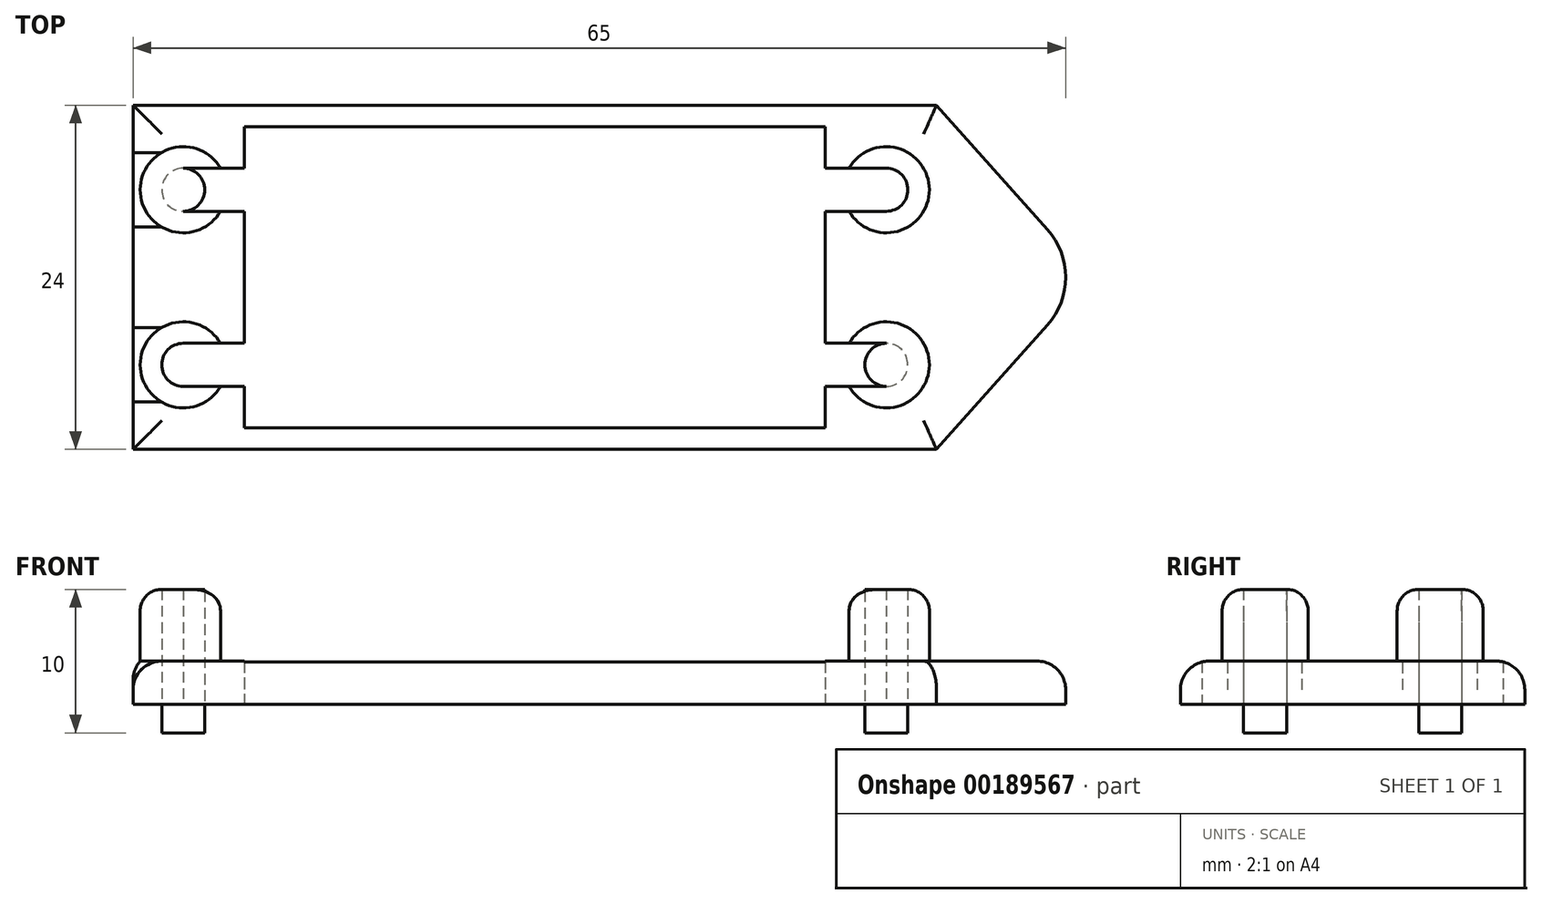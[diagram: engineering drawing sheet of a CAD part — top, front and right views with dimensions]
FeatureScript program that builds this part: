
annotation { "Feature Type Name" : "Feature", "Feature Type Description" : "" }
export const myFeature = defineFeature(function(context is Context, id is Id, definition is map)
    precondition{}
    {
        {
            var Q0;
            Q0=qCreatedBy(makeId("Top.planeOp"),FACE);
            var sketch = newSketch(context, id + "F0", { "sketchPlane" : qUnion([Q0])});
            skLineSegment(sketch, "E0.bottom", {"start": v(20.25, -10.5) * mm, "end": v(-20.25, -10.5) * mm});
            skLineSegment(sketch, "E0.top", {"start": v(20.25, 10.5) * mm, "end": v(-20.25, 10.5) * mm});
            skLineSegment(sketch, "E0.left", {"start": v(20.25, -10.5) * mm, "end": v(20.25, -7.6) * mm});
            skLineSegment(sketch, "E0.right", {"start": v(-20.25, -10.5) * mm, "end": v(-20.25, -7.6) * mm});
            skPoint(sketch, "E0.middle", {"position": v(0, 0) * mm});
            skArc(sketch, "E1", {"start": v(-24.5, 7.6) * mm, "mid": v(-26, 6.1) * mm, "end": v(-24.5, 4.6) * mm});
            skLineSegment(sketch, "E2", {"start": v(-24.5, 4.6) * mm, "end": v(-20.25, 4.6) * mm});
            skLineSegment(sketch, "E3", {"start": v(-20.25, 7.6) * mm, "end": v(-24.5, 7.6) * mm});
            skLineSegment(sketch, "E4.trimOffspring", {"start": v(-20.25, 7.6) * mm, "end": v(-20.25, 10.5) * mm});
            skLineSegment(sketch, "E5.MirrorCS", {"start": v(20.25, 7.6) * mm, "end": v(24.5, 7.6) * mm});
            skLineSegment(sketch, "E6.MirrorCS", {"start": v(20.25, 7.6) * mm, "end": v(20.25, 10.5) * mm});
            skLineSegment(sketch, "E7.MirrorCS", {"start": v(24.5, 4.6) * mm, "end": v(20.25, 4.6) * mm});
            skArc(sketch, "E8.MirrorCS", {"start": v(24.5, 7.6) * mm, "mid": v(26, 6.1) * mm, "end": v(24.5, 4.6) * mm});
            skLineSegment(sketch, "E9.MirrorCS", {"start": v(24.5, -4.6) * mm, "end": v(20.25, -4.6) * mm});
            skArc(sketch, "E10.MirrorCS", {"start": v(24.5, -7.6) * mm, "mid": v(26, -6.1) * mm, "end": v(24.5, -4.6) * mm});
            skLineSegment(sketch, "E11.MirrorCS", {"start": v(20.25, -7.6) * mm, "end": v(24.5, -7.6) * mm});
            skLineSegment(sketch, "E12.MirrorCS", {"start": v(-20.25, 10.5) * mm, "end": v(-20.25, 7.6) * mm});
            skLineSegment(sketch, "E13.MirrorCS", {"start": v(-20.25, -7.6) * mm, "end": v(-24.5, -7.6) * mm});
            skLineSegment(sketch, "E14.MirrorCS", {"start": v(-24.5, -4.6) * mm, "end": v(-20.25, -4.6) * mm});
            skArc(sketch, "E15.MirrorCS", {"start": v(-24.5, -7.6) * mm, "mid": v(-26, -6.1) * mm, "end": v(-24.5, -4.6) * mm});
            skLineSegment(sketch, "E16.MirrorCS", {"start": v(-20.25, -7.6) * mm, "end": v(-20.25, -10.5) * mm});
            skLineSegment(sketch, "E17.trimOffspring", {"start": v(20.25, -4.6) * mm, "end": v(20.25, 4.6) * mm});
            skLineSegment(sketch, "E18.trimOffspring", {"start": v(-20.25, -4.6) * mm, "end": v(-20.25, 4.6) * mm});
            skLineSegment(sketch, "E19.trimOffspring", {"start": v(-20.25, 4.6) * mm, "end": v(-20.25, -4.6) * mm});
            skSolve(sketch);
        }
        {
            var Q0;
            Q0=makeQuery(id+"F0.imprint","IMPRINT",FACE,{"disambiguationData":[TD([[makeQuery(id+"F0.imprint","IMPRINT",EDGE,{"derivedFrom":sQuery(id+"F0.wireOp",EDGE,"E0.bottom")}),-1.0]])]});
            extrude(context, id + "F1", {"entities" : qUnion([Q0]), "depth" : 2 * mm});
        }
        {
            var Q0;
            Q0=makeQuery(id+"F1.opExtrude","CAP_FACE",FACE,{"disambiguationData":[OSD([sQuery(id+"F0.wireOp",EDGE,"E0.bottom"),sQuery(id+"F0.wireOp",EDGE,"E0.top"),sQuery(id+"F0.wireOp",EDGE,"E0.left"),sQuery(id+"F0.wireOp",EDGE,"E0.right")])],"isStart":false});
            var sketch = newSketch(context, id + "F2", { "sketchPlane" : qUnion([Q0])});
            skLineSegment(sketch, "E20.bottom", {"start": v(28, -12) * mm, "end": v(-28, -12) * mm});
            skLineSegment(sketch, "E20.top", {"start": v(28, 12) * mm, "end": v(-28, 12) * mm});
            skLineSegment(sketch, "E20.right", {"start": v(-28, -12) * mm, "end": v(-28, 12) * mm});
            skPoint(sketch, "E20.middle", {"position": v(0, 0) * mm});
            skCircle(sketch, "E21", {"center": v(32, 0) * mm, "radius": 1 * mm, "construction": true});
            skArc(sketch, "E22", {"start": v(35.73, -3.33) * mm, "mid": v(37, 0) * mm, "end": v(35.73, 3.33) * mm});
            skLineSegment(sketch, "E23", {"start": v(28, -12) * mm, "end": v(35.73, -3.33) * mm});
            skLineSegment(sketch, "E24", {"start": v(28, 12) * mm, "end": v(35.73, 3.33) * mm});
            skSolve(sketch);
        }
        {
            var Q0;
            Q0=makeQuery(id+"F2.imprint","IMPRINT",FACE,{"disambiguationData":[TD([[makeQuery(id+"F2.imprint","IMPRINT",EDGE,{"derivedFrom":sQuery(id+"F2.wireOp",EDGE,"E20.bottom")}),-1.0]])]});
            var Q1;
            Q1=makeQuery(id+"F2.imprint","IMPRINT",FACE,{"disambiguationData":[TD([[makeQuery(id+"F2.imprint","IMPRINT",EDGE,{"derivedFrom":makeQuery(id+"F1.opExtrude","CAP_EDGE",EDGE,{"disambiguationData":[OSD([sQuery(id+"F0.wireOp",EDGE,"E0.bottom")])],"isStart":false})}),-1.0]])]});
            extrude(context, id + "F3", {"entities" : qUnion([Q0, Q1]), "operationType" : NewBodyOperationType.ADD, "depth" : 3 * mm});
        }
        {
            var Q0;
            Q0=makeQuery(id+"F1.opExtrude","CAP_FACE",FACE,{"disambiguationData":[OSD([sQuery(id+"F0.wireOp",EDGE,"E0.bottom"),sQuery(id+"F0.wireOp",EDGE,"E0.top"),sQuery(id+"F0.wireOp",EDGE,"E1"),sQuery(id+"F0.wireOp",EDGE,"E2"),sQuery(id+"F0.wireOp",EDGE,"E3"),sQuery(id+"F0.wireOp",EDGE,"E5.MirrorCS"),sQuery(id+"F0.wireOp",EDGE,"E7.MirrorCS"),sQuery(id+"F0.wireOp",EDGE,"E0.left"),sQuery(id+"F0.wireOp",EDGE,"E8.MirrorCS"),sQuery(id+"F0.wireOp",EDGE,"E9.MirrorCS"),sQuery(id+"F0.wireOp",EDGE,"E10.MirrorCS"),sQuery(id+"F0.wireOp",EDGE,"E11.MirrorCS"),sQuery(id+"F0.wireOp",EDGE,"E12.MirrorCS"),sQuery(id+"F0.wireOp",EDGE,"E13.MirrorCS"),sQuery(id+"F0.wireOp",EDGE,"E14.MirrorCS"),sQuery(id+"F0.wireOp",EDGE,"E15.MirrorCS"),sQuery(id+"F0.wireOp",EDGE,"E16.MirrorCS"),sQuery(id+"F0.wireOp",EDGE,"E6.MirrorCS"),sQuery(id+"F0.wireOp",EDGE,"E17.trimOffspring"),sQuery(id+"F0.wireOp",EDGE,"E19.trimOffspring")])],"isStart":true});
            var sketch = newSketch(context, id + "F4", { "sketchPlane" : qUnion([Q0])});
            skCircle(sketch, "E25", {"center": v(24.5, -6.1) * mm, "radius": 1.5 * mm});
            skCircle(sketch, "E26", {"center": v(24.5, 6.1) * mm, "radius": 1.5 * mm});
            skCircle(sketch, "E27", {"center": v(-24.5, -6.1) * mm, "radius": 1.5 * mm});
            skCircle(sketch, "E28", {"center": v(-24.5, 6.1) * mm, "radius": 1.5 * mm});
            skSolve(sketch);
        }
        {
            var Q0;
            Q0=makeQuery(id+"F3.opExtrude","CAP_FACE",FACE,{"disambiguationData":[OSD([sQuery(id+"F2.wireOp",EDGE,"E20.bottom"),sQuery(id+"F2.wireOp",EDGE,"E20.top"),sQuery(id+"F2.wireOp",EDGE,"E20.right"),sQuery(id+"F2.wireOp",EDGE,"E22"),sQuery(id+"F2.wireOp",EDGE,"E23"),sQuery(id+"F2.wireOp",EDGE,"E24")])],"isStart":false});
            var sketch = newSketch(context, id + "F5", { "sketchPlane" : qUnion([Q0])});
            skCircle(sketch, "E29", {"center": v(-24.5, 6.1) * mm, "radius": 3 * mm});
            skCircle(sketch, "E30", {"center": v(-24.5, -6.1) * mm, "radius": 3 * mm});
            skCircle(sketch, "E31", {"center": v(24.5, 6.1) * mm, "radius": 3 * mm});
            skCircle(sketch, "E32", {"center": v(24.5, -6.1) * mm, "radius": 3 * mm});
            skSolve(sketch);
        }
        {
            var Q0;
            Q0=makeQuery(id+"F5.imprint","IMPRINT",FACE,{"disambiguationData":[TD([[makeQuery(id+"F5.imprint","IMPRINT",EDGE,{"derivedFrom":sQuery(id+"F5.wireOp",EDGE,"E29")}),1.0]])]});
            var Q1;
            Q1=makeQuery(id+"F5.imprint","IMPRINT",FACE,{"disambiguationData":[TD([[makeQuery(id+"F5.imprint","IMPRINT",EDGE,{"derivedFrom":sQuery(id+"F5.wireOp",EDGE,"E30")}),1.0]])]});
            var Q2;
            Q2=makeQuery(id+"F5.imprint","IMPRINT",FACE,{"disambiguationData":[TD([[makeQuery(id+"F5.imprint","IMPRINT",EDGE,{"derivedFrom":sQuery(id+"F5.wireOp",EDGE,"E32")}),1.0]])]});
            var Q3;
            Q3=makeQuery(id+"F5.imprint","IMPRINT",FACE,{"disambiguationData":[TD([[makeQuery(id+"F5.imprint","IMPRINT",EDGE,{"derivedFrom":sQuery(id+"F5.wireOp",EDGE,"E31")}),1.0]])]});
            extrude(context, id + "F6", {"entities" : qUnion([Q0, Q1, Q2, Q3]), "operationType" : NewBodyOperationType.ADD, "depth" : 5 * mm});
        }
        {
            var Q0;
            Q0=makeQuery(id+"F3.opExtrude","CAP_EDGE",EDGE,{"disambiguationData":[OSD([sQuery(id+"F2.wireOp",EDGE,"E20.top")])],"isStart":false});
            var Q1;
            Q1=makeQuery(id+"F3.opExtrude","CAP_EDGE",EDGE,{"disambiguationData":[OSD([sQuery(id+"F2.wireOp",EDGE,"E20.right")])],"isStart":false});
            var Q2;
            Q2=makeQuery(id+"F3.opExtrude","CAP_EDGE",EDGE,{"disambiguationData":[OSD([sQuery(id+"F2.wireOp",EDGE,"E20.bottom")])],"isStart":false});
            var Q3;
            Q3=makeQuery(id+"F3.opExtrude","CAP_EDGE",EDGE,{"disambiguationData":[OSD([sQuery(id+"F2.wireOp",EDGE,"E23")])],"isStart":false});
            fillet(context, id + "F7", {"entities" : qUnion([Q0, Q1, Q2, Q3]), "radius" : 2 * mm, "tangentPropagation" : true, "allowEdgeOverflow" : false});
        }
        {
            var Q0;
            Q0=makeQuery(id+"F1.opExtrude","SWEPT_EDGE",EDGE,{"disambiguationData":[OSD([sQuery(id+"F0.wireOp",EDGE,"E0.top"),sQuery(id+"F0.wireOp",EDGE,"E6.MirrorCS")])]});
            var Q1;
            Q1=makeQuery(id+"F1.opExtrude","SWEPT_EDGE",EDGE,{"disambiguationData":[OSD([sQuery(id+"F0.wireOp",EDGE,"E0.top"),sQuery(id+"F0.wireOp",EDGE,"E12.MirrorCS")])]});
            var Q2;
            Q2=makeQuery(id+"F1.opExtrude","SWEPT_EDGE",EDGE,{"disambiguationData":[OSD([sQuery(id+"F0.wireOp",EDGE,"E0.bottom"),sQuery(id+"F0.wireOp",EDGE,"E0.left")])]});
            var Q3;
            Q3=makeQuery(id+"F1.opExtrude","SWEPT_EDGE",EDGE,{"disambiguationData":[OSD([sQuery(id+"F0.wireOp",EDGE,"E0.bottom"),sQuery(id+"F0.wireOp",EDGE,"E16.MirrorCS")])]});
            fillet(context, id + "F8", {"entities" : qUnion([Q0, Q1, Q2, Q3]), "radius" : 1 * mm, "tangentPropagation" : true, "allowEdgeOverflow" : false});
        }
        {
            var Q0;
            {var subQ0=sQuery(id+"F4.wireOp",EDGE,"E27");Q0=makeQuery(id+"F4.imprint","IMPRINT",FACE,{"disambiguationData":[TD([[makeQuery(id+"F4.imprint","IMPRINT",EDGE,{"disambiguationData":[OD(0.0)],"derivedFrom":subQ0}),-1.0]])]});}
            var Q1;
            {var subQ0=sQuery(id+"F4.wireOp",EDGE,"E28");var subQ1=makeQuery(id+"F4.imprint","INTERSECT",VERTEX,{"derivedFrom":[makeQuery(id+"F1.opExtrude","CAP_EDGE",EDGE,{"disambiguationData":[OSD([sQuery(id+"F0.wireOp",EDGE,"E13.MirrorCS")])],"isStart":true}),subQ0]});Q1=makeQuery(id+"F4.imprint","IMPRINT",FACE,{"disambiguationData":[TD([[makeQuery(id+"F4.imprint","IMPRINT",EDGE,{"disambiguationData":[TD([[subQ1,-1.0]])],"derivedFrom":subQ0}),1.0]])]});}
            var Q2;
            {var subQ0=sQuery(id+"F4.wireOp",EDGE,"E25");var subQ1=makeQuery(id+"F4.imprint","INTERSECT",VERTEX,{"derivedFrom":[makeQuery(id+"F1.opExtrude","CAP_EDGE",EDGE,{"disambiguationData":[OSD([sQuery(id+"F0.wireOp",EDGE,"E5.MirrorCS")])],"isStart":true}),subQ0]});Q2=makeQuery(id+"F4.imprint","IMPRINT",FACE,{"disambiguationData":[TD([[makeQuery(id+"F4.imprint","IMPRINT",EDGE,{"disambiguationData":[TD([[subQ1,-1.0]])],"derivedFrom":subQ0}),1.0]])]});}
            var Q3;
            {var subQ0=sQuery(id+"F4.wireOp",EDGE,"E26");Q3=makeQuery(id+"F4.imprint","IMPRINT",FACE,{"disambiguationData":[TD([[makeQuery(id+"F4.imprint","IMPRINT",EDGE,{"disambiguationData":[OD(0.0)],"derivedFrom":subQ0}),-1.0]])]});}
            extrude(context, id + "F9", {"entities" : qUnion([Q0, Q1, Q2, Q3]), "operationType" : NewBodyOperationType.REMOVE, "endBound" : BoundingType.THROUGH_ALL, "oppositeDirection" : true, "depth" : 25 * mm});
        }
        {
            var Q0;
            Q0=makeQuery(id+"F6.opExtrude","CAP_EDGE",EDGE,{"disambiguationData":[OSD([sQuery(id+"F5.wireOp",EDGE,"E30")])],"isStart":false});
            var Q1;
            Q1=makeQuery(id+"F6.opExtrude","CAP_EDGE",EDGE,{"disambiguationData":[OSD([sQuery(id+"F5.wireOp",EDGE,"E29")])],"isStart":false});
            var Q2;
            Q2=makeQuery(id+"F6.opExtrude","CAP_EDGE",EDGE,{"disambiguationData":[OSD([sQuery(id+"F5.wireOp",EDGE,"E31")])],"isStart":false});
            var Q3;
            Q3=makeQuery(id+"F6.opExtrude","CAP_EDGE",EDGE,{"disambiguationData":[OSD([sQuery(id+"F5.wireOp",EDGE,"E32")])],"isStart":false});
            fillet(context, id + "F10", {"entities" : qUnion([Q0, Q1, Q2, Q3]), "radius" : 1.5 * mm, "tangentPropagation" : true, "allowEdgeOverflow" : false});
        }
    });
